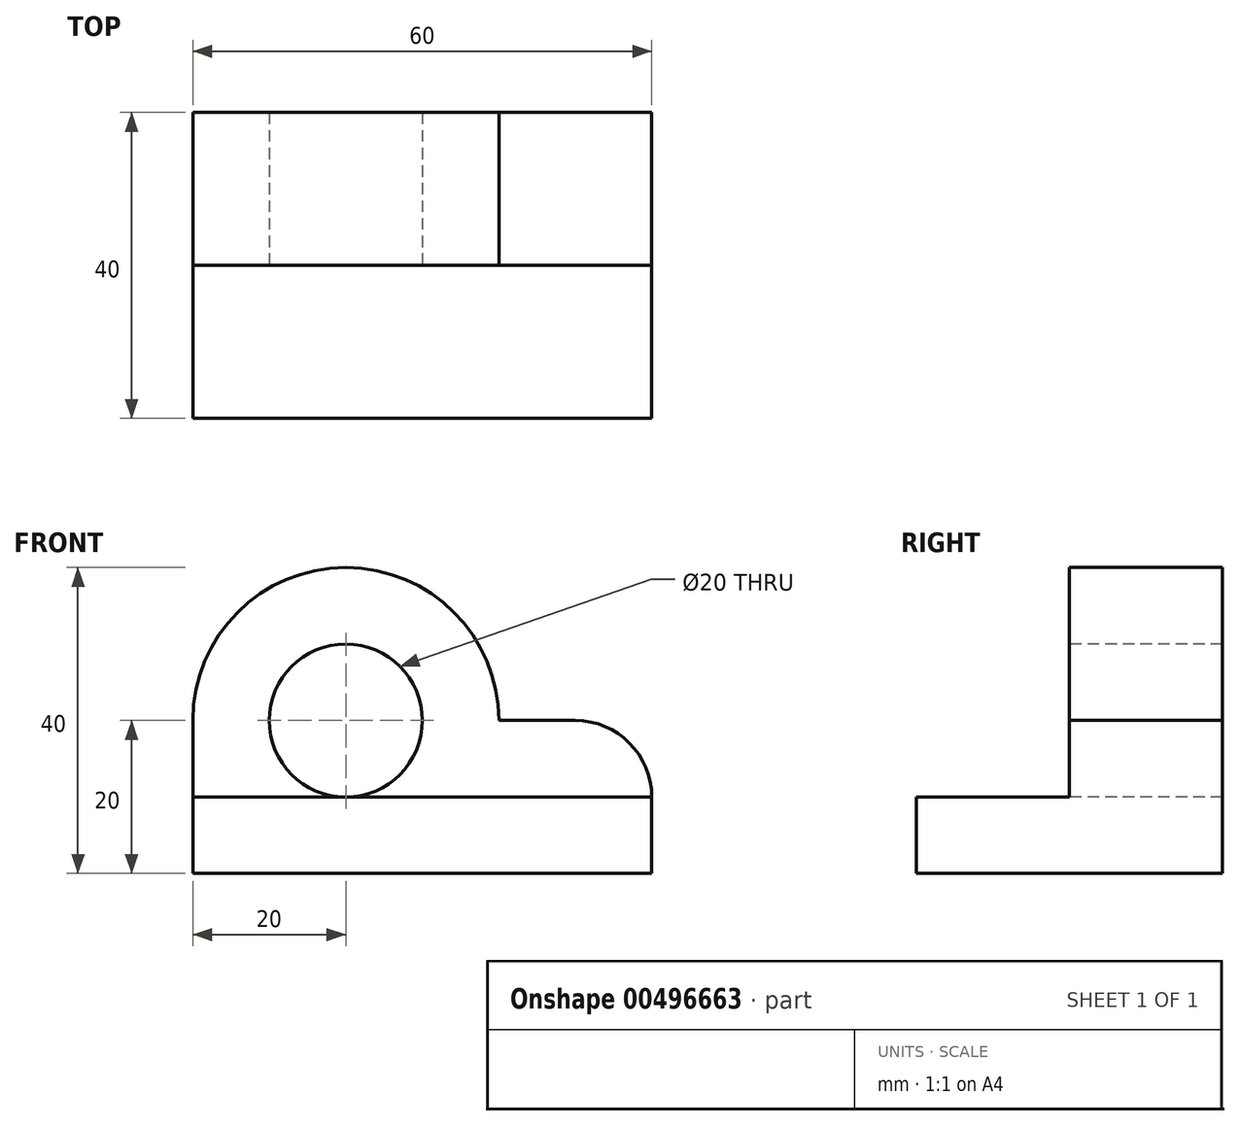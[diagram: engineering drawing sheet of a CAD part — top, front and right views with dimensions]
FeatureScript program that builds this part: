
annotation { "Feature Type Name" : "Feature", "Feature Type Description" : "" }
export const myFeature = defineFeature(function(context is Context, id is Id, definition is map)
    precondition{}
    {
        {
            var Q0;
            Q0=qCreatedBy(makeId("Front.planeOp"),FACE);
            var sketch = newSketch(context, id + "F0", { "sketchPlane" : qUnion([Q0])});
            skLineSegment(sketch, "E0", {"start": v(0, 0) * mm, "end": v(60, 0) * mm});
            skLineSegment(sketch, "E1", {"start": v(60, 0) * mm, "end": v(60, 10) * mm});
            skLineSegment(sketch, "E2", {"start": v(60, 10) * mm, "end": v(0, 10) * mm});
            skLineSegment(sketch, "E3", {"start": v(0, 10) * mm, "end": v(0, 0) * mm});
            skSolve(sketch);
        }
        {
            var Q0;
            Q0 = qSketchRegion(id + "F0", true);
            extrude(context, id + "F1", {"entities" : qUnion([Q0]), "depth" : 40 * mm});
        }
        {
            var Q0;
            Q0=makeQuery(id+"F1.opExtrude","SWEPT_FACE",FACE,{"disambiguationData":[OSD([sQuery(id+"F0.wireOp",EDGE,"E2")])]});
            var sketch = newSketch(context, id + "F2", { "sketchPlane" : qUnion([Q0])});
            skLineSegment(sketch, "E4.bottom", {"start": v(60, 0) * mm, "end": v(0, 0) * mm});
            skLineSegment(sketch, "E4.top", {"start": v(60, -20) * mm, "end": v(0, -20) * mm});
            skLineSegment(sketch, "E4.left", {"start": v(60, 0) * mm, "end": v(60, -20) * mm});
            skLineSegment(sketch, "E4.right", {"start": v(0, 0) * mm, "end": v(0, -20) * mm});
            skSolve(sketch);
        }
        {
            var Q0;
            Q0 = qSketchRegion(id + "F2", true);
            extrude(context, id + "F3", {"entities" : qUnion([Q0]), "operationType" : NewBodyOperationType.ADD, "depth" : 10 * mm});
        }
        {
            var Q0;
            Q0=makeQuery(id+"F3.opExtrude","CAP_FACE",FACE,{"disambiguationData":[OSD([sQuery(id+"F2.wireOp",EDGE,"E4.bottom"),sQuery(id+"F2.wireOp",EDGE,"E4.top"),sQuery(id+"F2.wireOp",EDGE,"E4.left"),sQuery(id+"F2.wireOp",EDGE,"E4.right")])],"isStart":false});
            var sketch = newSketch(context, id + "F4", { "sketchPlane" : qUnion([Q0])});
            skLineSegment(sketch, "E5.bottom", {"start": v(0, 0) * mm, "end": v(40, 0) * mm});
            skLineSegment(sketch, "E5.top", {"start": v(0, -20) * mm, "end": v(40, -20) * mm});
            skLineSegment(sketch, "E5.left", {"start": v(0, 0) * mm, "end": v(0, -20) * mm});
            skLineSegment(sketch, "E5.right", {"start": v(40, 0) * mm, "end": v(40, -20) * mm});
            skSolve(sketch);
        }
        {
            var Q0;
            Q0 = qSketchRegion(id + "F4", true);
            extrude(context, id + "F5", {"entities" : qUnion([Q0]), "operationType" : NewBodyOperationType.ADD, "depth" : 20 * mm});
        }
        {
            var Q0;
            Q0=makeQuery(id+"F5.opExtrude","CAP_EDGE",EDGE,{"disambiguationData":[OSD([sQuery(id+"F4.wireOp",EDGE,"E5.left")])],"isStart":false});
            var Q1;
            Q1=makeQuery(id+"F5.opExtrude","CAP_EDGE",EDGE,{"disambiguationData":[OSD([sQuery(id+"F4.wireOp",EDGE,"E5.right")])],"isStart":false});
            fillet(context, id + "F6", {"entities" : qUnion([Q0, Q1]), "radius" : 20 * mm, "tangentPropagation" : true, "allowEdgeOverflow" : false});
        }
        {
            var Q0;
            Q0=makeQuery(id+"F3.opExtrude","CAP_EDGE",EDGE,{"disambiguationData":[OSD([sQuery(id+"F2.wireOp",EDGE,"E4.left")])],"isStart":false});
            fillet(context, id + "F7", {"entities" : qUnion([Q0]), "radius" : 10 * mm, "tangentPropagation" : true, "allowEdgeOverflow" : false});
        }
        {
            var Q0;
            Q0=makeQuery(id+"F5.boolean.opBoolean","MERGE",FACE,{"derivedFrom":[makeQuery(id+"F3.opExtrude","SWEPT_FACE",FACE,{"disambiguationData":[OSD([sQuery(id+"F2.wireOp",EDGE,"E4.top")])]}),makeQuery(id+"F5.opExtrude","SWEPT_FACE",FACE,{"disambiguationData":[OSD([sQuery(id+"F4.wireOp",EDGE,"E5.top")])]})]});
            var sketch = newSketch(context, id + "F8", { "sketchPlane" : qUnion([Q0])});
            skCircle(sketch, "E6", {"center": v(20, 20) * mm, "radius": 10 * mm});
            skSolve(sketch);
        }
        {
            var Q0;
            Q0 = qSketchRegion(id + "F8", true);
            extrude(context, id + "F9", {"entities" : qUnion([Q0]), "operationType" : NewBodyOperationType.REMOVE, "oppositeDirection" : true, "depth" : 25 * mm});
        }
    });
